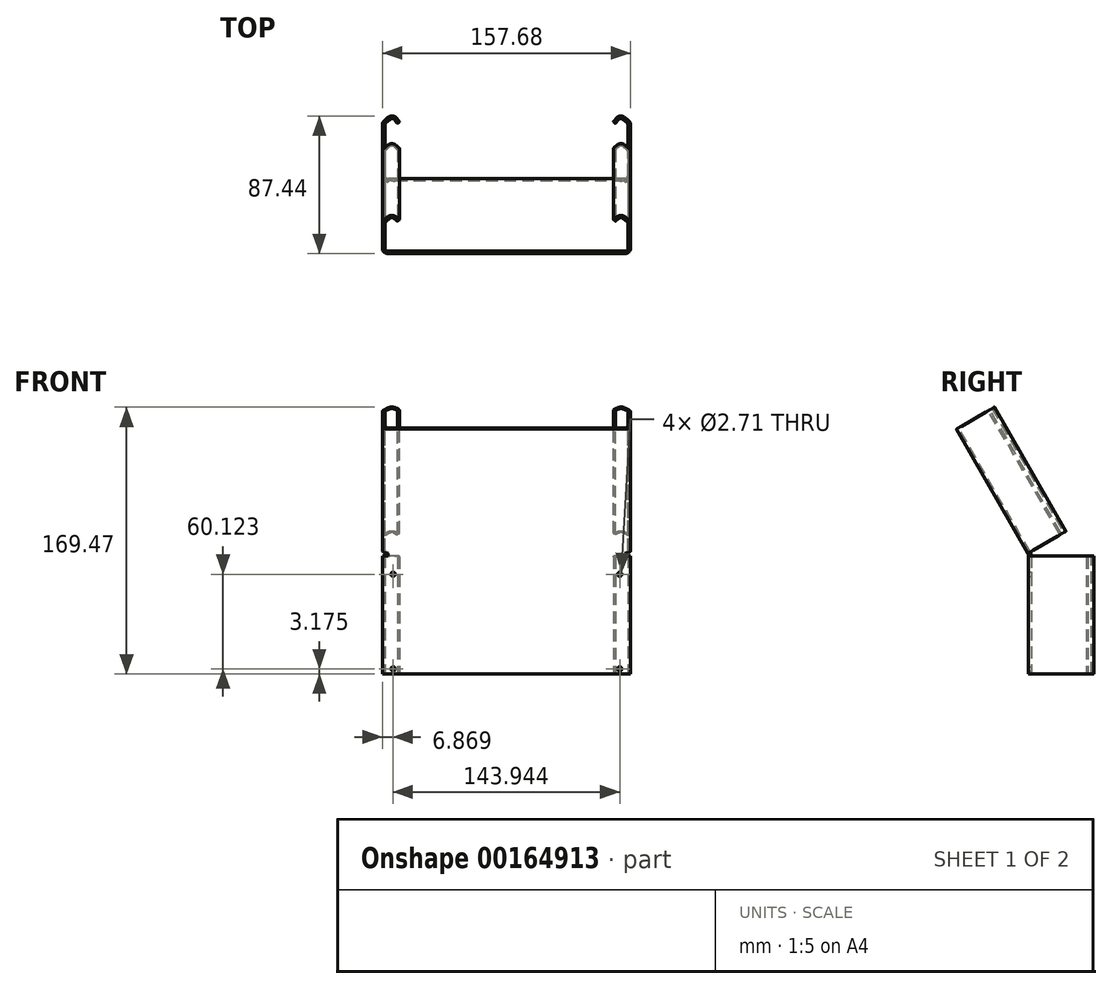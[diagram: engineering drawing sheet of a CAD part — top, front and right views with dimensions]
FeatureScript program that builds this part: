
annotation { "Feature Type Name" : "Feature", "Feature Type Description" : "" }
export const myFeature = defineFeature(function(context is Context, id is Id, definition is map)
    precondition{}
    {
        {
            var Q0;
            Q0=qCreatedBy(makeId("Top.planeOp"),FACE);
            var sketch = newSketch(context, id + "F0", { "sketchPlane" : qUnion([Q0])});
            skLineSegment(sketch, "E0", {"start": v(0, 0) * mm, "end": v(4.63, 3.93) * mm});
            skLineSegment(sketch, "E1", {"start": v(4.63, 3.93) * mm, "end": v(7.97, 0) * mm});
            skLineSegment(sketch, "E2", {"start": v(7.97, 0) * mm, "end": v(9.27, 1.1) * mm});
            skLineSegment(sketch, "E3", {"start": v(9.27, 1.1) * mm, "end": v(4.83, 6.34) * mm});
            skLineSegment(sketch, "E4", {"start": v(4.83, 6.34) * mm, "end": v(-1.7, 0.8) * mm});
            skLineSegment(sketch, "E5", {"start": v(0, 0) * mm, "end": v(0, -34.91) * mm});
            skLineSegment(sketch, "E6", {"start": v(0, -34.91) * mm, "end": v(154.26, -34.91) * mm});
            skLineSegment(sketch, "E7", {"start": v(155.97, -36.62) * mm, "end": v(-1.7, -36.62) * mm});
            skLineSegment(sketch, "E8", {"start": v(-1.7, -36.62) * mm, "end": v(-1.7, 0.8) * mm});
            skLineSegment(sketch, "E9", {"start": v(2.32, 1.97) * mm, "end": v(1.21, 3.27) * mm, "construction": true});
            skLineSegment(sketch, "E10", {"start": v(0, -34.91) * mm, "end": v(-1.7, -34.91) * mm, "construction": true});
            skLineSegment(sketch, "E11", {"start": v(77.13, -36.62) * mm, "end": v(77.13, -34.91) * mm, "construction": true});
            skLineSegment(sketch, "E12", {"start": v(154.26, -34.91) * mm, "end": v(154.26, 0) * mm});
            skLineSegment(sketch, "E13", {"start": v(154.26, 0) * mm, "end": v(149.63, 3.93) * mm});
            skLineSegment(sketch, "E14", {"start": v(149.63, 3.93) * mm, "end": v(146.29, 0) * mm});
            skLineSegment(sketch, "E15", {"start": v(146.29, 0) * mm, "end": v(144.99, 1.1) * mm});
            skLineSegment(sketch, "E16", {"start": v(144.99, 1.1) * mm, "end": v(149.43, 6.34) * mm});
            skLineSegment(sketch, "E17", {"start": v(149.43, 6.34) * mm, "end": v(155.97, 0.8) * mm});
            skLineSegment(sketch, "E18", {"start": v(155.97, 0.8) * mm, "end": v(155.97, -36.62) * mm});
            skArc(sketch, "E19", {"start": v(7.22, 3.53) * mm, "mid": v(4.7, 4.82) * mm, "end": v(2.01, 3.95) * mm, "construction": true});
            skArc(sketch, "E20", {"start": v(-0.4, 1.9) * mm, "mid": v(-1.37, 0.63) * mm, "end": v(-1.7, -0.92) * mm, "construction": true});
            skLineSegment(sketch, "E21", {"start": v(4.83, 6.34) * mm, "end": v(149.43, 6.34) * mm, "construction": true});
            skSolve(sketch);
        }
        {
            var Q0;
            Q0=qSketchRegion(id+"F0",true);
            extrude(context, id + "F1", {"entities" : qUnion([Q0]), "depth" : 74.9 * mm});
        }
        {
            var Q0;
            Q0=makeQuery(id+"F1.opExtrude","SWEPT_FACE",FACE,{"disambiguationData":[OSD([sQuery(id+"F0.wireOp",EDGE,"E6")])]});
            var sketch = newSketch(context, id + "F2", { "sketchPlane" : qUnion([Q0])});
            skLineSegment(sketch, "E22.bottom", {"start": v(0, 0) * mm, "end": v(-5.16, 0) * mm, "construction": true});
            skLineSegment(sketch, "E22.top", {"start": v(0, 3.17) * mm, "end": v(-5.16, 3.18) * mm, "construction": true});
            skLineSegment(sketch, "E22.left", {"start": v(0, 0) * mm, "end": v(0, 3.18) * mm, "construction": true});
            skLineSegment(sketch, "E22.right", {"start": v(-5.16, 0) * mm, "end": v(-5.16, 3.17) * mm, "construction": true});
            skLineSegment(sketch, "E23", {"start": v(-77.13, 0) * mm, "end": v(-77.13, 33.24) * mm, "construction": true});
            skLineSegment(sketch, "E24.bottom", {"start": v(-5.16, 3.17) * mm, "end": v(-149.1, 3.18) * mm, "construction": true});
            skLineSegment(sketch, "E24.top", {"start": v(-5.16, 63.3) * mm, "end": v(-149.1, 63.3) * mm, "construction": true});
            skLineSegment(sketch, "E24.left", {"start": v(-5.16, 3.17) * mm, "end": v(-5.16, 63.3) * mm, "construction": true});
            skLineSegment(sketch, "E24.right", {"start": v(-149.1, 3.18) * mm, "end": v(-149.1, 63.3) * mm, "construction": true});
            skPoint(sketch, "E24.middle", {"position": v(-77.13, 33.24) * mm});
            skCircle(sketch, "E25", {"center": v(-5.16, 3.17) * mm, "radius": 1.35 * mm});
            skCircle(sketch, "E26", {"center": v(-5.16, 63.3) * mm, "radius": 1.35 * mm});
            skCircle(sketch, "E27", {"center": v(-149.1, 63.3) * mm, "radius": 1.35 * mm});
            skCircle(sketch, "E28", {"center": v(-149.1, 3.18) * mm, "radius": 1.35 * mm});
            skSolve(sketch);
        }
        {
            var Q0;
            Q0=qSketchRegion(id+"F2",true);
            var Q1;
            Q1=makeQuery(id+"F1.opExtrude","SWEPT_FACE",FACE,{"disambiguationData":[OSD([sQuery(id+"F0.wireOp",EDGE,"E7")])]});
            extrude(context, id + "F3", {"entities" : qUnion([Q0]), "operationType" : NewBodyOperationType.REMOVE, "endBound" : BoundingType.UP_TO_SURFACE, "oppositeDirection" : true, "endBoundEntityFace" : qUnion([Q1]), "depth" : 25.4 * mm});
        }
        {
            var Q0;
            Q0=makeQuery(id+"F1.opExtrude","SWEPT_FACE",FACE,{"disambiguationData":[OSD([sQuery(id+"F0.wireOp",EDGE,"E5")])]});
            cPlane(context, id + "F4", {"entities" : qUnion([Q0]), "cplaneType" : CPlaneType.OFFSET, "offset" : 1.98 * mm, "width" : 152.4 * mm, "height" : 152.4 * mm});
        }
        {
            var Q0;
            Q0=makeQuery(id+"F1.opExtrude","SWEPT_FACE",FACE,{"disambiguationData":[OSD([sQuery(id+"F0.wireOp",EDGE,"E12")])]});
            cPlane(context, id + "F5", {"entities" : qUnion([Q0]), "cplaneType" : CPlaneType.OFFSET, "offset" : 1.98 * mm, "width" : 152.4 * mm, "height" : 152.4 * mm});
        }
        {
            assignVariable(context, id + "F6", {"name" : "x", "anyValue" : 91.08 * mm});
        }
        {
            var Q0;
            Q0=qCreatedBy(id+"F4.planeOp",FACE);
            var sketch = newSketch(context, id + "F7", { "sketchPlane" : qUnion([Q0])});
            skArc(sketch, "E29", {"start": v(-34.91, 74.9) * mm, "mid": v(-35.08, 76.2) * mm, "end": v(-35.59, 77.42) * mm});
            skArc(sketch, "E30", {"start": v(-36.62, 74.9) * mm, "mid": v(-36.74, 75.76) * mm, "end": v(-37.07, 76.57) * mm});
            skLineSegment(sketch, "E31", {"start": v(-35.59, 77.42) * mm, "end": v(-81.13, 156.3) * mm});
            skLineSegment(sketch, "E32", {"start": v(-81.13, 156.3) * mm, "end": v(-82.6, 155.44) * mm});
            skLineSegment(sketch, "E33", {"start": v(-37.07, 76.57) * mm, "end": v(-82.6, 155.44) * mm});
            skLineSegment(sketch, "E34", {"start": v(-36.62, 74.9) * mm, "end": v(-82.6, 74.9) * mm, "construction": true});
            skLineSegment(sketch, "E35", {"start": v(-82.6, 74.9) * mm, "end": v(-82.6, 155.44) * mm, "construction": true});
            skLineSegment(sketch, "E36", {"start": v(-34.91, 74.9) * mm, "end": v(-36.62, 74.9) * mm});
            skSolve(sketch);
        }
        {
            var Q0;
            Q0 = qSketchRegion(id + "F7", true);
            var Q1;
            Q1=qCreatedBy(id+"F5.planeOp",FACE);
            extrude(context, id + "F8", {"entities" : qUnion([Q0]), "operationType" : NewBodyOperationType.ADD, "endBound" : BoundingType.UP_TO_SURFACE, "endBoundEntityFace" : qUnion([Q1]), "depth" : 25.4 * mm});
        }
        {
            var Q0;
            Q0=makeQuery(id+"F8.opExtrude","SWEPT_FACE",FACE,{"disambiguationData":[OSD([sQuery(id+"F7.wireOp",EDGE,"E32")])]});
            var sketch = newSketch(context, id + "F9", { "sketchPlane" : qUnion([Q0])});
            skLineSegment(sketch, "E37.bottom", {"start": v(1.98, 6.18) * mm, "end": v(-1.7, 6.18) * mm});
            skLineSegment(sketch, "E37.top", {"start": v(1.98, 7.89) * mm, "end": v(0, 7.89) * mm});
            skLineSegment(sketch, "E37.left", {"start": v(1.98, 6.18) * mm, "end": v(1.98, 7.89) * mm});
            skLineSegment(sketch, "E38.bottom", {"start": v(152.28, 6.18) * mm, "end": v(155.97, 6.18) * mm});
            skLineSegment(sketch, "E38.top", {"start": v(152.28, 7.89) * mm, "end": v(154.26, 7.89) * mm});
            skLineSegment(sketch, "E38.left", {"start": v(152.28, 6.18) * mm, "end": v(152.28, 7.89) * mm});
            skLineSegment(sketch, "E39.left", {"start": v(154.26, 7.89) * mm, "end": v(154.26, 29) * mm});
            skLineSegment(sketch, "E39.right", {"start": v(155.97, 6.18) * mm, "end": v(155.97, 29.7) * mm});
            skLineSegment(sketch, "E40.left", {"start": v(-1.7, 6.18) * mm, "end": v(-1.7, 29.7) * mm});
            skLineSegment(sketch, "E40.right", {"start": v(0, 7.89) * mm, "end": v(0, 29) * mm});
            skLineSegment(sketch, "E41", {"start": v(154.26, 29) * mm, "end": v(149.9, 33.35) * mm});
            skLineSegment(sketch, "E42", {"start": v(149.9, 33.35) * mm, "end": v(146.26, 29.7) * mm});
            skLineSegment(sketch, "E43", {"start": v(146.26, 29.7) * mm, "end": v(145.05, 30.91) * mm});
            skLineSegment(sketch, "E44", {"start": v(145.05, 30.91) * mm, "end": v(149.9, 35.77) * mm});
            skLineSegment(sketch, "E45", {"start": v(149.9, 35.77) * mm, "end": v(155.97, 29.7) * mm});
            skLineSegment(sketch, "E46", {"start": v(0, 29) * mm, "end": v(4.36, 33.35) * mm});
            skLineSegment(sketch, "E47", {"start": v(4.36, 33.35) * mm, "end": v(8, 29.7) * mm});
            skLineSegment(sketch, "E48", {"start": v(-1.7, 29.7) * mm, "end": v(4.36, 35.77) * mm});
            skLineSegment(sketch, "E49", {"start": v(4.36, 35.77) * mm, "end": v(9.21, 30.91) * mm});
            skLineSegment(sketch, "E50", {"start": v(9.21, 30.91) * mm, "end": v(8, 29.7) * mm});
            skLineSegment(sketch, "E51", {"start": v(154.26, 29) * mm, "end": v(155.47, 30.2) * mm, "construction": true});
            skSolve(sketch);
        }
        {
            var Q0;
            Q0=makeQuery(id+"F9.imprint","IMPRINT",FACE,{"disambiguationData":[TD([[makeQuery(id+"F9.imprint","IMPRINT",EDGE,{"derivedFrom":sQuery(id+"F9.wireOp",EDGE,"E37.bottom")}),-1.0]])]});
            var Q1;
            Q1=makeQuery(id+"F9.imprint","IMPRINT",FACE,{"disambiguationData":[TD([[makeQuery(id+"F9.imprint","IMPRINT",EDGE,{"derivedFrom":sQuery(id+"F9.wireOp",EDGE,"E38.bottom")}),1.0]])]});
            extrude(context, id + "F10", {"entities" : qUnion([Q0, Q1]), "operationType" : NewBodyOperationType.ADD, "oppositeDirection" : true, "depth" : (getVariable(context, 'x'))});
        }
        {
            var Q0;
            Q0=makeQuery(id+"F1.opExtrude","SWEPT_EDGE",EDGE,{"disambiguationData":[OSD([sQuery(id+"F0.wireOp",EDGE,"E16"),sQuery(id+"F0.wireOp",EDGE,"E17")])]});
            var Q1;
            Q1=makeQuery(id+"F1.opExtrude","SWEPT_EDGE",EDGE,{"disambiguationData":[OSD([sQuery(id+"F0.wireOp",EDGE,"E17"),sQuery(id+"F0.wireOp",EDGE,"E18")])]});
            var Q2;
            Q2=makeQuery(id+"F1.opExtrude","SWEPT_EDGE",EDGE,{"disambiguationData":[OSD([sQuery(id+"F0.wireOp",EDGE,"E7"),sQuery(id+"F0.wireOp",EDGE,"E18")])]});
            var Q3;
            Q3=makeQuery(id+"F1.opExtrude","SWEPT_EDGE",EDGE,{"disambiguationData":[OSD([sQuery(id+"F0.wireOp",EDGE,"E7"),sQuery(id+"F0.wireOp",EDGE,"E8")])]});
            var Q4;
            Q4=makeQuery(id+"F1.opExtrude","SWEPT_EDGE",EDGE,{"disambiguationData":[OSD([sQuery(id+"F0.wireOp",EDGE,"E4"),sQuery(id+"F0.wireOp",EDGE,"E8")])]});
            var Q5;
            Q5=makeQuery(id+"F1.opExtrude","SWEPT_EDGE",EDGE,{"disambiguationData":[OSD([sQuery(id+"F0.wireOp",EDGE,"E3"),sQuery(id+"F0.wireOp",EDGE,"E4")])]});
            var Q6;
            Q6=makeQuery(id+"F10.opExtrude","SWEPT_EDGE",EDGE,{"disambiguationData":[OSD([sQuery(id+"F9.wireOp",EDGE,"E44"),sQuery(id+"F9.wireOp",EDGE,"E45")])]});
            var Q7;
            Q7=makeQuery(id+"F10.opExtrude","SWEPT_EDGE",EDGE,{"disambiguationData":[OSD([sQuery(id+"F9.wireOp",EDGE,"E39.right"),sQuery(id+"F9.wireOp",EDGE,"E45")])]});
            var Q8;
            Q8=makeQuery(id+"F10.opExtrude","SWEPT_EDGE",EDGE,{"disambiguationData":[OSD([sQuery(id+"F9.wireOp",EDGE,"E38.bottom"),sQuery(id+"F9.wireOp",EDGE,"E39.right")])]});
            var Q9;
            Q9=makeQuery(id+"F10.opExtrude","SWEPT_EDGE",EDGE,{"disambiguationData":[OSD([sQuery(id+"F9.wireOp",EDGE,"E37.bottom"),sQuery(id+"F9.wireOp",EDGE,"E40.left")])]});
            var Q10;
            Q10=makeQuery(id+"F10.opExtrude","SWEPT_EDGE",EDGE,{"disambiguationData":[OSD([sQuery(id+"F9.wireOp",EDGE,"E40.left"),sQuery(id+"F9.wireOp",EDGE,"E48")])]});
            var Q11;
            Q11=makeQuery(id+"F10.opExtrude","SWEPT_EDGE",EDGE,{"disambiguationData":[OSD([sQuery(id+"F9.wireOp",EDGE,"E48"),sQuery(id+"F9.wireOp",EDGE,"E49")])]});
            fillet(context, id + "F11", {"entities" : qUnion([Q0, Q1, Q2, Q3, Q4, Q5, Q6, Q7, Q8, Q9, Q10, Q11]), "radius" : 3.7 * mm, "tangentPropagation" : true, "allowEdgeOverflow" : false});
        }
        {
            var Q0;
            Q0=makeQuery(id+"F1.opExtrude","SWEPT_EDGE",EDGE,{"disambiguationData":[OSD([sQuery(id+"F0.wireOp",EDGE,"E13"),sQuery(id+"F0.wireOp",EDGE,"E14")])]});
            var Q1;
            Q1=makeQuery(id+"F1.opExtrude","SWEPT_EDGE",EDGE,{"disambiguationData":[OSD([sQuery(id+"F0.wireOp",EDGE,"E12"),sQuery(id+"F0.wireOp",EDGE,"E13")])]});
            var Q2;
            Q2=makeQuery(id+"F1.opExtrude","SWEPT_EDGE",EDGE,{"disambiguationData":[OSD([sQuery(id+"F0.wireOp",EDGE,"E6"),sQuery(id+"F0.wireOp",EDGE,"E12")])]});
            var Q3;
            Q3=makeQuery(id+"F1.opExtrude","SWEPT_EDGE",EDGE,{"disambiguationData":[OSD([sQuery(id+"F0.wireOp",EDGE,"E5"),sQuery(id+"F0.wireOp",EDGE,"E6")])]});
            var Q4;
            Q4=makeQuery(id+"F1.opExtrude","SWEPT_EDGE",EDGE,{"disambiguationData":[OSD([sQuery(id+"F0.wireOp",EDGE,"E0"),sQuery(id+"F0.wireOp",EDGE,"E5")])]});
            var Q5;
            Q5=makeQuery(id+"F1.opExtrude","SWEPT_EDGE",EDGE,{"disambiguationData":[OSD([sQuery(id+"F0.wireOp",EDGE,"E0"),sQuery(id+"F0.wireOp",EDGE,"E1")])]});
            var Q6;
            Q6=makeQuery(id+"F10.opExtrude","SWEPT_EDGE",EDGE,{"disambiguationData":[OSD([sQuery(id+"F9.wireOp",EDGE,"E40.right"),sQuery(id+"F9.wireOp",EDGE,"E46")])]});
            var Q7;
            Q7=makeQuery(id+"F10.opExtrude","SWEPT_EDGE",EDGE,{"disambiguationData":[OSD([sQuery(id+"F9.wireOp",EDGE,"E46"),sQuery(id+"F9.wireOp",EDGE,"E47")])]});
            var Q8;
            Q8=makeQuery(id+"F10.opExtrude","SWEPT_EDGE",EDGE,{"disambiguationData":[OSD([sQuery(id+"F9.wireOp",EDGE,"E37.top"),sQuery(id+"F9.wireOp",EDGE,"E40.right")])]});
            var Q9;
            Q9=makeQuery(id+"F10.opExtrude","SWEPT_EDGE",EDGE,{"disambiguationData":[OSD([sQuery(id+"F9.wireOp",EDGE,"E38.top"),sQuery(id+"F9.wireOp",EDGE,"E39.left")])]});
            var Q10;
            Q10=makeQuery(id+"F10.opExtrude","SWEPT_EDGE",EDGE,{"disambiguationData":[OSD([sQuery(id+"F9.wireOp",EDGE,"E39.left"),sQuery(id+"F9.wireOp",EDGE,"E41")])]});
            var Q11;
            Q11=makeQuery(id+"F10.opExtrude","SWEPT_EDGE",EDGE,{"disambiguationData":[OSD([sQuery(id+"F9.wireOp",EDGE,"E41"),sQuery(id+"F9.wireOp",EDGE,"E42")])]});
            fillet(context, id + "F12", {"entities" : qUnion([Q0, Q1, Q2, Q3, Q4, Q5, Q6, Q7, Q8, Q9, Q10, Q11]), "radius" : 1.98 * mm, "tangentPropagation" : true, "allowEdgeOverflow" : false});
        }
        {
            var Q0;
            Q0=makeQuery(id+"F1.opExtrude","CAP_EDGE",EDGE,{"disambiguationData":[OSD([sQuery(id+"F0.wireOp",EDGE,"E15")])],"isStart":false});
            var Q1;
            Q1=makeQuery(id+"F1.opExtrude","CAP_EDGE",EDGE,{"disambiguationData":[OSD([sQuery(id+"F0.wireOp",EDGE,"E15")])],"isStart":true});
            var Q2;
            Q2=makeQuery(id+"F1.opExtrude","CAP_EDGE",EDGE,{"disambiguationData":[OSD([sQuery(id+"F0.wireOp",EDGE,"E2")])],"isStart":true});
            var Q3;
            Q3=makeQuery(id+"F1.opExtrude","CAP_EDGE",EDGE,{"disambiguationData":[OSD([sQuery(id+"F0.wireOp",EDGE,"E2")])],"isStart":false});
            var Q4;
            Q4=makeQuery(id+"F10.opExtrude","CAP_EDGE",EDGE,{"disambiguationData":[OSD([sQuery(id+"F9.wireOp",EDGE,"E50")])],"isStart":true});
            var Q5;
            Q5=makeQuery(id+"F10.opExtrude","CAP_EDGE",EDGE,{"disambiguationData":[OSD([sQuery(id+"F9.wireOp",EDGE,"E50")])],"isStart":false});
            var Q6;
            Q6=makeQuery(id+"F10.opExtrude","CAP_EDGE",EDGE,{"disambiguationData":[OSD([sQuery(id+"F9.wireOp",EDGE,"E43")])],"isStart":false});
            var Q7;
            Q7=makeQuery(id+"F10.opExtrude","CAP_EDGE",EDGE,{"disambiguationData":[OSD([sQuery(id+"F9.wireOp",EDGE,"E43")])],"isStart":true});
            fillet(context, id + "F13", {"entities" : qUnion([Q0, Q1, Q2, Q3, Q4, Q5, Q6, Q7]), "radius" : 0.76 * mm, "tangentPropagation" : true, "allowEdgeOverflow" : false});
        }
    });
